# Revit family: 511_PW_DBS_nailfin
name_source: partatom
category: Windows
units: mm (PartAtom-declared; Revit-internal decimal feet)

## family parameters
Always vertical = Yes
Cut with Voids When Loaded = No
Host = Wall
OmniClass Number = 23.30.20.00
OmniClass Title = Windows
Room Calculation Point = No
Shared = No

## types (187) — shared parameters
Default Sill Height = 31 1/2"
Wall Closure = By host

## per-type parameters (varying)
| type | Height | MLW | Width |
| 24x24 | 24" | 3" | 24" |
| 60x60 | 60" | 7 1/2" | 60" |
| 12x12Min | 12" | 1 1/2" | 12" |
| 60x120Max | 120" | 7 1/2" | 60" |
| 72x100Max | 100" | 9" | 72" |
| 36x36 | 36" | 4 1/2" | 36" |
| 48x48 | 48" | 6" | 48" |
| 72x72 | 72" | 9" | 72" |
| 84x84 | 84" | 10 1/2" | 84" |
| 12x24 | 24" | 1 1/2" | 12" |
| 12x30 | 30" | 1 1/2" | 12" |
| 12x36 | 36" | 1 1/2" | 12" |
| 12x42 | 42" | 1 1/2" | 12" |
| 12x48 | 48" | 1 1/2" | 12" |
| 12x54 | 54" | 1 1/2" | 12" |
| 12x60 | 60" | 1 1/2" | 12" |
| 24x12 | 12" | 3" | 24" |
| 24x30 | 30" | 3" | 24" |
| 12x18 | 18" | 1 1/2" | 12" |
| 24x18 | 18" | 3" | 24" |
| 24x36 | 36" | 3" | 24" |
| 24x42 | 42" | 3" | 24" |
| 24x48 | 48" | 3" | 24" |
| 24x54 | 54" | 3" | 24" |
| 24x60 | 60" | 3" | 24" |
| 24x66 | 66" | 3" | 24" |
| 24x72 | 72" | 3" | 24" |
| 24x78 | 78" | 3" | 24" |
| 30x12 | 12" | 3 3/4" | 30" |
| 18x12 | 12" | 2 1/4" | 18" |
| 18x18 | 18" | 2 1/4" | 18" |
| 18x24 | 24" | 2 1/4" | 18" |
| 18x30 | 30" | 2 1/4" | 18" |
| 18x36 | 36" | 2 1/4" | 18" |
| 18x42 | 42" | 2 1/4" | 18" |
| 18x48 | 48" | 2 1/4" | 18" |
| 18x54 | 54" | 2 1/4" | 18" |
| 18x60 | 60" | 2 1/4" | 18" |
| 18x66 | 66" | 2 1/4" | 18" |
| 30x18 | 18" | 3 3/4" | 30" |
| 30x24 | 24" | 3 3/4" | 30" |
| 30x30 | 30" | 3 3/4" | 30" |
| 30x36 | 36" | 3 3/4" | 30" |
| 30x42 | 42" | 3 3/4" | 30" |
| 30x48 | 48" | 3 3/4" | 30" |
| 30x54 | 54" | 3 3/4" | 30" |
| 30x60 | 60" | 3 3/4" | 30" |
| 30x66 | 66" | 3 3/4" | 30" |
| 30x72 | 72" | 3 3/4" | 30" |
| 30x78 | 78" | 3 3/4" | 30" |
| 30x84 | 84" | 3 3/4" | 30" |
| 30x90 | 90" | 3 3/4" | 30" |
| 30x96 | 96" | 3 3/4" | 30" |
| 36x12 | 12" | 4 1/2" | 36" |
| 36x18 | 18" | 4 1/2" | 36" |
| 36x24 | 24" | 4 1/2" | 36" |
| 36x30 | 30" | 4 1/2" | 36" |
| 36x42 | 42" | 4 1/2" | 36" |
| 36x48 | 48" | 4 1/2" | 36" |
| 36x54 | 54" | 4 1/2" | 36" |
| 36x60 | 60" | 4 1/2" | 36" |
| 36x66 | 66" | 4 1/2" | 36" |
| 36x72 | 72" | 4 1/2" | 36" |
| 36x78 | 78" | 4 1/2" | 36" |
| 36x84 | 84" | 4 1/2" | 36" |
| 36x90 | 90" | 4 1/2" | 36" |
| 36x96 | 96" | 4 1/2" | 36" |
| 36x102 | 102" | 4 1/2" | 36" |
| 42x12 | 12" | 5 1/4" | 42" |
| 42x18 | 18" | 5 1/4" | 42" |
| 42x24 | 24" | 5 1/4" | 42" |
| 42x30 | 30" | 5 1/4" | 42" |
| 42x36 | 36" | 5 1/4" | 42" |
| 42x42 | 42" | 5 1/4" | 42" |
| 42x48 | 48" | 5 1/4" | 42" |
| 42x54 | 54" | 5 1/4" | 42" |
| 42x60 | 60" | 5 1/4" | 42" |
| 42x66 | 66" | 5 1/4" | 42" |
| 42x72 | 72" | 5 1/4" | 42" |
| 42x78 | 78" | 5 1/4" | 42" |
| 42x84 | 84" | 5 1/4" | 42" |
| 42x90 | 90" | 5 1/4" | 42" |
| 42x96 | 96" | 5 1/4" | 42" |
| 42x102 | 102" | 5 1/4" | 42" |
| 42x108 | 108" | 5 1/4" | 42" |
| 42x114 | 114" | 5 1/4" | 42" |
| 42x120 | 120" | 5 1/4" | 42" |
| 48x12 | 12" | 6" | 48" |
| 48x18 | 18" | 6" | 48" |
| 48x24 | 24" | 6" | 48" |
| 48x30 | 30" | 6" | 48" |
| 48x36 | 36" | 6" | 48" |
| 48x42 | 42" | 6" | 48" |
| 48x54 | 54" | 6" | 48" |
| 48x60 | 60" | 6" | 48" |
| 48x66 | 66" | 6" | 48" |
| 48x72 | 72" | 6" | 48" |
| 48x78 | 78" | 6" | 48" |
| 48x84 | 84" | 6" | 48" |
| 48x90 | 90" | 6" | 48" |
| 48x96 | 96" | 6" | 48" |
| 48x102 | 102" | 6" | 48" |
| 48x108 | 108" | 6" | 48" |
| 48x114 | 114" | 6" | 48" |
| 48x120 | 120" | 6" | 48" |
| 54x12 | 12" | 6 3/4" | 54" |
| 54x18 | 18" | 6 3/4" | 54" |
| 54x24 | 24" | 6 3/4" | 54" |
| 54x30 | 30" | 6 3/4" | 54" |
| 54x36 | 36" | 6 3/4" | 54" |
| 54x42 | 42" | 6 3/4" | 54" |
| 54x48 | 48" | 6 3/4" | 54" |
| 54x54 | 54" | 6 3/4" | 54" |
| 54x60 | 60" | 6 3/4" | 54" |
| 54x66 | 66" | 6 3/4" | 54" |
| 54x72 | 72" | 6 3/4" | 54" |
| 54x78 | 78" | 6 3/4" | 54" |
| 54x84 | 84" | 6 3/4" | 54" |
| 54x90 | 90" | 6 3/4" | 54" |
| 54x96 | 96" | 6 3/4" | 54" |
| 54x102 | 102" | 6 3/4" | 54" |
| 54x108 | 108" | 6 3/4" | 54" |
| 54x114 | 114" | 6 3/4" | 54" |
| 54x120 | 120" | 6 3/4" | 54" |
| 60x18 | 18" | 7 1/2" | 60" |
| 60x24 | 24" | 7 1/2" | 60" |
| 60x30 | 30" | 7 1/2" | 60" |
| 60x36 | 36" | 7 1/2" | 60" |
| 60x42 | 42" | 7 1/2" | 60" |
| 60x48 | 48" | 7 1/2" | 60" |
| 60x54 | 54" | 7 1/2" | 60" |
| 60x66 | 66" | 7 1/2" | 60" |
| 60x72 | 72" | 7 1/2" | 60" |
| 60x78 | 78" | 7 1/2" | 60" |
| 60x84 | 84" | 7 1/2" | 60" |
| 60x90 | 90" | 7 1/2" | 60" |
| 60x96 | 96" | 7 1/2" | 60" |
| 60x102 | 102" | 7 1/2" | 60" |
| 60x108 | 108" | 7 1/2" | 60" |
| 60x114 | 114" | 7 1/2" | 60" |
| 66x24 | 24" | 8 1/4" | 66" |
| 66x30 | 30" | 8 1/4" | 66" |
| 66x36 | 36" | 8 1/4" | 66" |
| 66x42 | 42" | 8 1/4" | 66" |
| 66x48 | 48" | 8 1/4" | 66" |
| 66x54 | 54" | 8 1/4" | 66" |
| 66x60 | 60" | 8 1/4" | 66" |
| 66x66 | 66" | 8 1/4" | 66" |
| 66x72 | 72" | 8 1/4" | 66" |
| 66x78 | 78" | 8 1/4" | 66" |
| 66x84 | 84" | 8 1/4" | 66" |
| 66x90 | 90" | 8 1/4" | 66" |
| 66x96 | 96" | 8 1/4" | 66" |
| 66x102 | 102" | 8 1/4" | 66" |
| 66x108 | 108" | 8 1/4" | 66" |
| 72x30 | 30" | 9" | 72" |
| 72x36 | 36" | 9" | 72" |
| 72x42 | 42" | 9" | 72" |
| 72x48 | 48" | 9" | 72" |
| 72x54 | 54" | 9" | 72" |
| 72x60 | 60" | 9" | 72" |
| 72x66 | 66" | 9" | 72" |
| 72x78 | 78" | 9" | 72" |
| 72x84 | 84" | 9" | 72" |
| 72x90 | 90" | 9" | 72" |
| 72x96 | 96" | 9" | 72" |
| 78x90 | 90" | 9 3/4" | 78" |
| 78x36 | 36" | 9 3/4" | 78" |
| 78x42 | 42" | 9 3/4" | 78" |
| 78x48 | 48" | 9 3/4" | 78" |
| 78x54 | 54" | 9 3/4" | 78" |
| 78x60 | 60" | 9 3/4" | 78" |
| 78x66 | 66" | 9 3/4" | 78" |
| 78x72 | 72" | 9 3/4" | 78" |
| 78x78 | 78" | 9 3/4" | 78" |
| 78x84 | 84" | 9 3/4" | 78" |
| 84x42 | 42" | 10 1/2" | 84" |
| 84x48 | 48" | 10 1/2" | 84" |
| 84x54 | 54" | 10 1/2" | 84" |
| 84x60 | 60" | 10 1/2" | 84" |
| 84x66 | 66" | 10 1/2" | 84" |
| 84x72 | 72" | 10 1/2" | 84" |
| 84x78 | 78" | 10 1/2" | 84" |
| 90x78 | 78" | 11 1/4" | 90" |
| 90x60 | 60" | 11 1/4" | 90" |
| 90x66 | 66" | 11 1/4" | 90" |
| 90x72 | 72" | 11 1/4" | 90" |

## geometry (parser evidence)
native form markers: Sweep x2
no freeform markers — native parametric forms only
